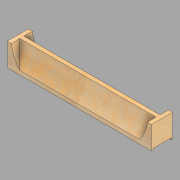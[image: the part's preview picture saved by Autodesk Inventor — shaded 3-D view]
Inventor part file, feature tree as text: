
AUTODESK INVENTOR PART (.ipt)
format: ipt  version: 2022.2 (Build 262287010, 287A)  size: 147,968 bytes
history: native  units: in
note: dims shown in document units (in); Inventor stores cm internally (conversion verified against a paired STEP export)
features: direct_edit x1, other x1, revolve x1
ambient origin geometry x8: Origin, YZ Plane, XZ Plane, XY Plane, X Axis, Y Axis, Z Axis, Center Point
bodies: Solid1 (feature_tree)
feature tree (3):
  direct_edit  "Direct Edit1"
  other  "West (6)"
  revolve  "Rotate1"  Angle=90.0deg
